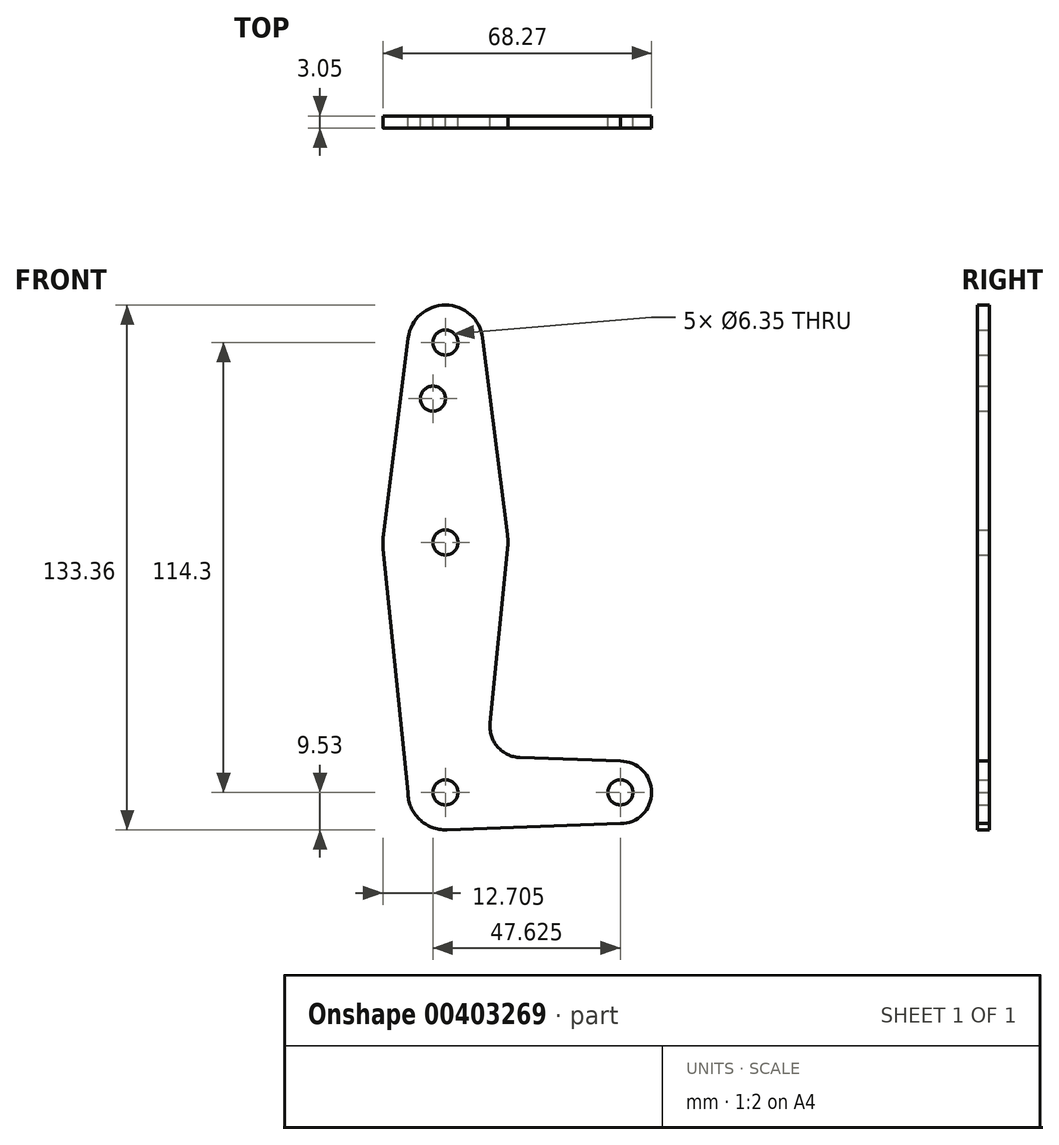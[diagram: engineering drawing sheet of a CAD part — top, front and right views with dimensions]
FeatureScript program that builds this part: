
annotation { "Feature Type Name" : "Feature", "Feature Type Description" : "" }
export const myFeature = defineFeature(function(context is Context, id is Id, definition is map)
    precondition{}
    {
        {
            var Q0;
            Q0=qCreatedBy(makeId("Front.planeOp"),FACE);
            var sketch = newSketch(context, id + "F0", { "sketchPlane" : qUnion([Q0])});
            skLineSegment(sketch, "E0", {"start": v(0, 114.3) * mm, "end": v(0, 0) * mm, "construction": true});
            skLineSegment(sketch, "E1", {"start": v(0, 0) * mm, "end": v(44.45, 0) * mm, "construction": true});
            skCircle(sketch, "E2", {"center": v(0, 114.3) * mm, "radius": 9.52 * mm});
            skCircle(sketch, "E3", {"center": v(0, 0) * mm, "radius": 9.53 * mm});
            skCircle(sketch, "E4", {"center": v(44.45, 0) * mm, "radius": 7.94 * mm});
            skCircle(sketch, "E5", {"center": v(0, 63.5) * mm, "radius": 15.88 * mm});
            skCircle(sketch, "E6", {"center": v(0, 114.3) * mm, "radius": 3.18 * mm});
            skCircle(sketch, "E7", {"center": v(0, 0) * mm, "radius": 3.18 * mm});
            skCircle(sketch, "E8", {"center": v(44.45, 0) * mm, "radius": 3.18 * mm});
            skCircle(sketch, "E9", {"center": v(0, 63.5) * mm, "radius": 3.18 * mm});
            skCircle(sketch, "E10", {"center": v(-3.18, 100.03) * mm, "radius": 3.18 * mm});
            skLineSegment(sketch, "E11", {"start": v(-9.45, 115.5) * mm, "end": v(-15.75, 65.48) * mm});
            skLineSegment(sketch, "E12", {"start": v(9.45, 115.5) * mm, "end": v(15.75, 65.48) * mm});
            skLineSegment(sketch, "E13", {"start": v(-9.53, 0) * mm, "end": v(-15.8, 61.9) * mm});
            skLineSegment(sketch, "E14", {"start": v(11.34, 17.6) * mm, "end": v(15.8, 61.9) * mm});
            skLineSegment(sketch, "E15", {"start": v(44.45, -7.94) * mm, "end": v(0, -9.53) * mm});
            skLineSegment(sketch, "E16", {"start": v(44.45, 7.94) * mm, "end": v(18.97, 8.85) * mm});
            skPoint(sketch, "E17.newPointA", {"position": v(0, 9.53) * mm});
            skArc(sketch, "E17.filletArc", {"start": v(11.34, 17.6) * mm, "mid": v(13.26, 11.57) * mm, "end": v(18.97, 8.85) * mm});
            skSolve(sketch);
        }
        {
            var Q0;
            Q0 = qSketchRegion(id + "F0", true);
            extrude(context, id + "F1", {"entities" : qUnion([Q0]), "depth" : 3.05 * mm});
        }
    });
